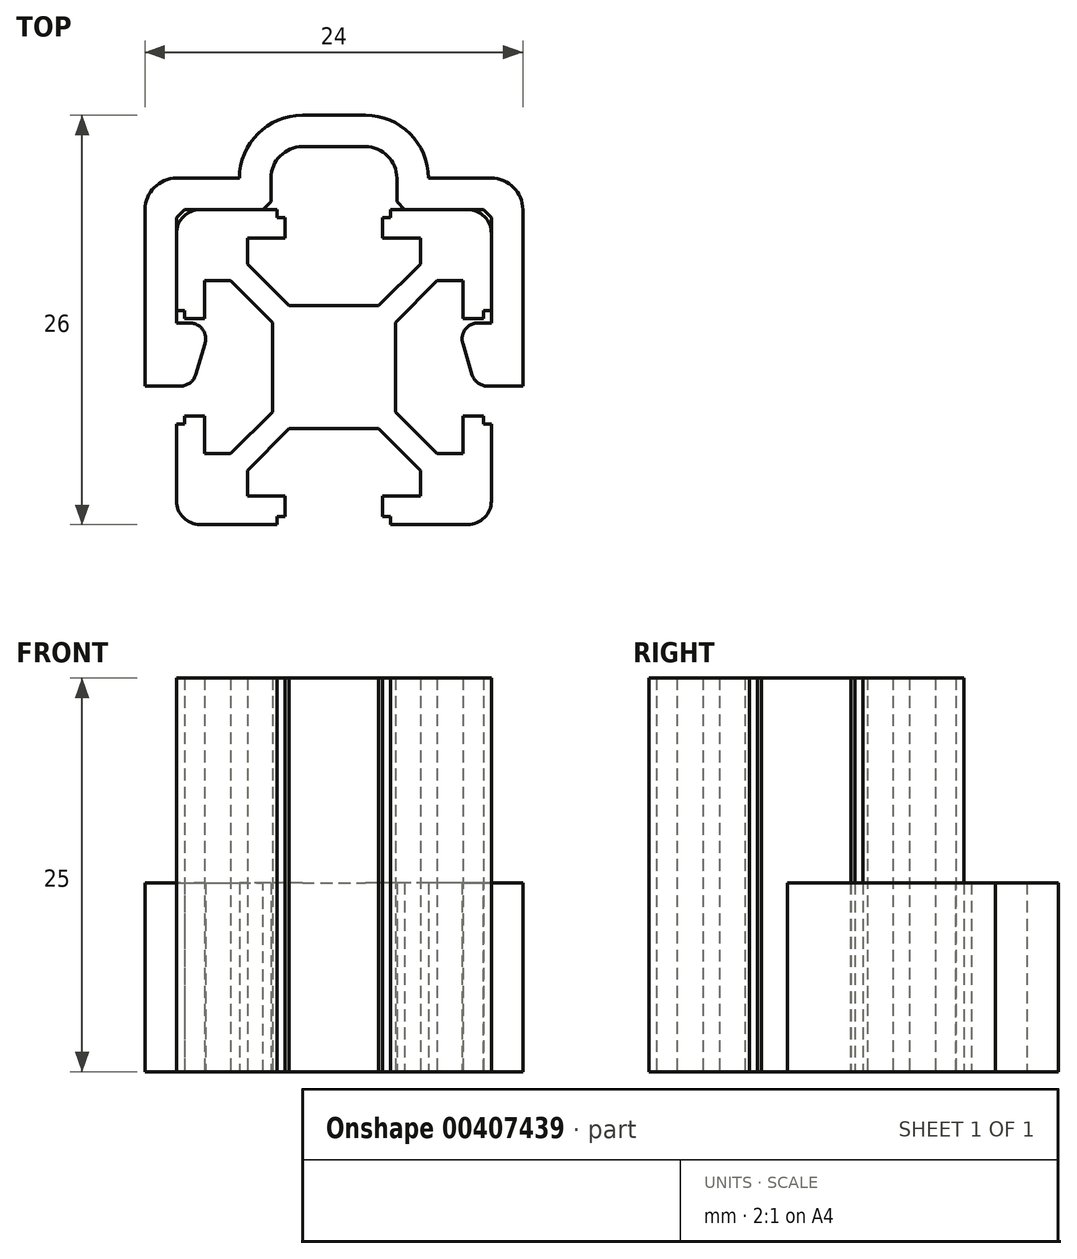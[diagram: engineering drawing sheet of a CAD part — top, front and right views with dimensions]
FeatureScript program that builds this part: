
annotation { "Feature Type Name" : "Feature", "Feature Type Description" : "" }
export const myFeature = defineFeature(function(context is Context, id is Id, definition is map)
    precondition{}
    {
        {
            var Q0;
            Q0=qCreatedBy(makeId("Top.planeOp"),FACE);
            var sketch = newSketch(context, id + "F0", { "sketchPlane" : qUnion([Q0])});
            skPoint(sketch, "E0", {"position": v(0, 0) * mm});
            skPoint(sketch, "E1", {"position": v(-3.9, 0) * mm});
            skLineSegment(sketch, "E2", {"start": v(-3.9, 0) * mm, "end": v(-3.9, 2.84) * mm});
            skLineSegment(sketch, "E3", {"start": v(-3.9, 2.84) * mm, "end": v(-6.56, 5.5) * mm});
            skLineSegment(sketch, "E4", {"start": v(-6.56, 5.5) * mm, "end": v(-8.2, 5.5) * mm});
            skLineSegment(sketch, "E5", {"start": v(-8.2, 5.5) * mm, "end": v(-8.2, 3.1) * mm});
            skLineSegment(sketch, "E6", {"start": v(-8.2, 3.1) * mm, "end": v(-9.5, 3.1) * mm});
            skLineSegment(sketch, "E7", {"start": v(-9.5, 3.1) * mm, "end": v(-9.5, 3.6) * mm});
            skLineSegment(sketch, "E8", {"start": v(-9.5, 3.6) * mm, "end": v(-10, 3.6) * mm});
            skLineSegment(sketch, "E9", {"start": v(-10, 3.6) * mm, "end": v(-10, 8.5) * mm});
            skLineSegment(sketch, "E10", {"start": v(-8.5, 10) * mm, "end": v(-3.6, 10) * mm});
            skLineSegment(sketch, "E11", {"start": v(-3.1, 9.5) * mm, "end": v(-3.1, 8.2) * mm});
            skLineSegment(sketch, "E12", {"start": v(-3.1, 8.2) * mm, "end": v(-5.5, 8.2) * mm});
            skLineSegment(sketch, "E13", {"start": v(-5.5, 8.2) * mm, "end": v(-5.5, 6.56) * mm});
            skLineSegment(sketch, "E14", {"start": v(-5.5, 6.56) * mm, "end": v(-2.84, 3.9) * mm});
            skLineSegment(sketch, "E15", {"start": v(-2.84, 3.9) * mm, "end": v(0, 3.9) * mm});
            skLineSegment(sketch, "E16", {"start": v(-3.6, 10) * mm, "end": v(-3.6, 9.5) * mm});
            skLineSegment(sketch, "E17", {"start": v(-3.6, 9.5) * mm, "end": v(-3.1, 9.5) * mm});
            skCircle(sketch, "E18", {"center": v(0, 0) * mm, "radius": 2.5 * mm});
            skPoint(sketch, "E19", {"position": v(0, 10) * mm});
            skPoint(sketch, "E19.positionSnap0", {"position": v(-6.8, 10) * mm});
            skPoint(sketch, "E20", {"position": v(-10, 0) * mm});
            skPoint(sketch, "E21.visualSharp", {"position": v(-10, 10) * mm});
            skArc(sketch, "E21.filletArc", {"start": v(-8.5, 10) * mm, "mid": v(-9.56, 9.56) * mm, "end": v(-10, 8.5) * mm});
            skPoint(sketch, "E22.visualSharp", {"position": v(-5.5, 6.56) * mm});
            skLineSegment(sketch, "E22.filletArc", {"start": v(-5.5, 6.56) * mm, "end": v(-5.5, 6.56) * mm});
            skPoint(sketch, "E23.visualSharp", {"position": v(-3.6, 10) * mm});
            skLineSegment(sketch, "E23.filletArc", {"start": v(-3.6, 10) * mm, "end": v(-3.6, 10) * mm});
            skPoint(sketch, "E24.visualSharp", {"position": v(-3.1, 9.5) * mm});
            skLineSegment(sketch, "E24.filletArc", {"start": v(-3.1, 9.5) * mm, "end": v(-3.1, 9.5) * mm});
            skPoint(sketch, "E25.visualSharp", {"position": v(-10, 3.6) * mm});
            skLineSegment(sketch, "E25.filletArc", {"start": v(-10, 3.6) * mm, "end": v(-10, 3.6) * mm});
            skLineSegment(sketch, "E26.1.0", {"start": v(-8.2, -3.1) * mm, "end": v(-8.2, -5.5) * mm});
            skLineSegment(sketch, "E26.1.1", {"start": v(-2.84, -3.9) * mm, "end": v(-5.5, -6.56) * mm});
            skLineSegment(sketch, "E26.1.2", {"start": v(0, -3.9) * mm, "end": v(-2.84, -3.9) * mm});
            skArc(sketch, "E26.1.3", {"start": v(-10, -8.5) * mm, "mid": v(-9.56, -9.56) * mm, "end": v(-8.5, -10) * mm});
            skLineSegment(sketch, "E26.1.4", {"start": v(-3.9, -2.84) * mm, "end": v(-3.9, 0) * mm});
            skPoint(sketch, "E26.1.5", {"position": v(0, -10) * mm});
            skPoint(sketch, "E26.1.7", {"position": v(-10, -10) * mm});
            skLineSegment(sketch, "E26.1.8", {"start": v(-5.5, -6.56) * mm, "end": v(-5.5, -8.2) * mm});
            skPoint(sketch, "E26.1.9", {"position": v(0, -3.9) * mm});
            skLineSegment(sketch, "E26.1.10", {"start": v(-6.56, -5.5) * mm, "end": v(-3.9, -2.84) * mm});
            skLineSegment(sketch, "E26.1.11", {"start": v(-8.2, -5.5) * mm, "end": v(-6.56, -5.5) * mm});
            skLineSegment(sketch, "E26.1.12", {"start": v(-9.5, -3.1) * mm, "end": v(-8.2, -3.1) * mm});
            skLineSegment(sketch, "E26.1.13", {"start": v(-5.5, -8.2) * mm, "end": v(-3.1, -8.2) * mm});
            skPoint(sketch, "E26.1.14", {"position": v(-10, -6.8) * mm});
            skLineSegment(sketch, "E26.1.15", {"start": v(-3.1, -8.2) * mm, "end": v(-3.1, -9.5) * mm});
            skLineSegment(sketch, "E26.1.17", {"start": v(-3.6, -10) * mm, "end": v(-8.5, -10) * mm});
            skLineSegment(sketch, "E26.1.18", {"start": v(-10, -8.5) * mm, "end": v(-10, -3.6) * mm});
            skPoint(sketch, "E26.1.19", {"position": v(-3.6, -10) * mm});
            skPoint(sketch, "E26.1.21", {"position": v(-9.5, -3.1) * mm});
            skPoint(sketch, "E26.1.22", {"position": v(-10, -3.6) * mm});
            skPoint(sketch, "E26.1.23", {"position": v(-6.56, -5.5) * mm});
            skLineSegment(sketch, "E26.1.24", {"start": v(-3.1, -9.5) * mm, "end": v(-3.6, -9.5) * mm});
            skLineSegment(sketch, "E26.1.25", {"start": v(-9.5, -3.6) * mm, "end": v(-9.5, -3.1) * mm});
            skLineSegment(sketch, "E26.1.26", {"start": v(-10, -3.6) * mm, "end": v(-9.5, -3.6) * mm});
            skLineSegment(sketch, "E26.1.27", {"start": v(-3.6, -9.5) * mm, "end": v(-3.6, -10) * mm});
            skLineSegment(sketch, "E26.2.0", {"start": v(3.1, -8.2) * mm, "end": v(5.5, -8.2) * mm});
            skLineSegment(sketch, "E26.2.1", {"start": v(3.9, -2.84) * mm, "end": v(6.56, -5.5) * mm});
            skLineSegment(sketch, "E26.2.2", {"start": v(3.9, 0) * mm, "end": v(3.9, -2.84) * mm});
            skArc(sketch, "E26.2.3", {"start": v(8.5, -10) * mm, "mid": v(9.56, -9.56) * mm, "end": v(10, -8.5) * mm});
            skLineSegment(sketch, "E26.2.4", {"start": v(2.84, -3.9) * mm, "end": v(0, -3.9) * mm});
            skPoint(sketch, "E26.2.5", {"position": v(10, 0) * mm});
            skPoint(sketch, "E26.2.6", {"position": v(0, -10) * mm});
            skPoint(sketch, "E26.2.7", {"position": v(10, -10) * mm});
            skLineSegment(sketch, "E26.2.8", {"start": v(6.56, -5.5) * mm, "end": v(8.2, -5.5) * mm});
            skPoint(sketch, "E26.2.9", {"position": v(3.9, 0) * mm});
            skLineSegment(sketch, "E26.2.10", {"start": v(5.5, -6.56) * mm, "end": v(2.84, -3.9) * mm});
            skLineSegment(sketch, "E26.2.11", {"start": v(5.5, -8.2) * mm, "end": v(5.5, -6.56) * mm});
            skLineSegment(sketch, "E26.2.12", {"start": v(3.1, -9.5) * mm, "end": v(3.1, -8.2) * mm});
            skLineSegment(sketch, "E26.2.13", {"start": v(8.2, -5.5) * mm, "end": v(8.2, -3.1) * mm});
            skPoint(sketch, "E26.2.14", {"position": v(6.8, -10) * mm});
            skLineSegment(sketch, "E26.2.15", {"start": v(8.2, -3.1) * mm, "end": v(9.5, -3.1) * mm});
            skLineSegment(sketch, "E26.2.17", {"start": v(10, -3.6) * mm, "end": v(10, -8.5) * mm});
            skLineSegment(sketch, "E26.2.18", {"start": v(8.5, -10) * mm, "end": v(3.6, -10) * mm});
            skPoint(sketch, "E26.2.19", {"position": v(10, -3.6) * mm});
            skPoint(sketch, "E26.2.21", {"position": v(3.1, -9.5) * mm});
            skPoint(sketch, "E26.2.22", {"position": v(3.6, -10) * mm});
            skPoint(sketch, "E26.2.23", {"position": v(5.5, -6.56) * mm});
            skLineSegment(sketch, "E26.2.24", {"start": v(9.5, -3.1) * mm, "end": v(9.5, -3.6) * mm});
            skLineSegment(sketch, "E26.2.25", {"start": v(3.6, -9.5) * mm, "end": v(3.1, -9.5) * mm});
            skLineSegment(sketch, "E26.2.26", {"start": v(3.6, -10) * mm, "end": v(3.6, -9.5) * mm});
            skLineSegment(sketch, "E26.2.27", {"start": v(9.5, -3.6) * mm, "end": v(10, -3.6) * mm});
            skLineSegment(sketch, "E26.3.0", {"start": v(8.2, 3.1) * mm, "end": v(8.2, 5.5) * mm});
            skLineSegment(sketch, "E26.3.1", {"start": v(2.84, 3.9) * mm, "end": v(5.5, 6.56) * mm});
            skLineSegment(sketch, "E26.3.2", {"start": v(0, 3.9) * mm, "end": v(2.84, 3.9) * mm});
            skArc(sketch, "E26.3.3", {"start": v(10, 8.5) * mm, "mid": v(9.56, 9.56) * mm, "end": v(8.5, 10) * mm});
            skLineSegment(sketch, "E26.3.4", {"start": v(3.9, 2.84) * mm, "end": v(3.9, 0) * mm});
            skPoint(sketch, "E26.3.6", {"position": v(10, 0) * mm});
            skPoint(sketch, "E26.3.7", {"position": v(10, 10) * mm});
            skLineSegment(sketch, "E26.3.8", {"start": v(5.5, 6.56) * mm, "end": v(5.5, 8.2) * mm});
            skPoint(sketch, "E26.3.9", {"position": v(0, 3.9) * mm});
            skLineSegment(sketch, "E26.3.10", {"start": v(6.56, 5.5) * mm, "end": v(3.9, 2.84) * mm});
            skLineSegment(sketch, "E26.3.11", {"start": v(8.2, 5.5) * mm, "end": v(6.56, 5.5) * mm});
            skLineSegment(sketch, "E26.3.12", {"start": v(9.5, 3.1) * mm, "end": v(8.2, 3.1) * mm});
            skLineSegment(sketch, "E26.3.13", {"start": v(5.5, 8.2) * mm, "end": v(3.1, 8.2) * mm});
            skPoint(sketch, "E26.3.14", {"position": v(10, 6.8) * mm});
            skLineSegment(sketch, "E26.3.15", {"start": v(3.1, 8.2) * mm, "end": v(3.1, 9.5) * mm});
            skLineSegment(sketch, "E26.3.17", {"start": v(3.6, 10) * mm, "end": v(8.5, 10) * mm});
            skLineSegment(sketch, "E26.3.18", {"start": v(10, 8.5) * mm, "end": v(10, 3.6) * mm});
            skPoint(sketch, "E26.3.19", {"position": v(3.6, 10) * mm});
            skPoint(sketch, "E26.3.21", {"position": v(9.5, 3.1) * mm});
            skPoint(sketch, "E26.3.22", {"position": v(10, 3.6) * mm});
            skPoint(sketch, "E26.3.23", {"position": v(6.56, 5.5) * mm});
            skLineSegment(sketch, "E26.3.24", {"start": v(3.1, 9.5) * mm, "end": v(3.6, 9.5) * mm});
            skLineSegment(sketch, "E26.3.25", {"start": v(9.5, 3.6) * mm, "end": v(9.5, 3.1) * mm});
            skLineSegment(sketch, "E26.3.26", {"start": v(10, 3.6) * mm, "end": v(9.5, 3.6) * mm});
            skLineSegment(sketch, "E26.3.27", {"start": v(3.6, 9.5) * mm, "end": v(3.6, 10) * mm});
            skSolve(sketch);
        }
        {
            var Q0;
            Q0=qCreatedBy(makeId("Top.planeOp"),FACE);
            var sketch = newSketch(context, id + "F1", { "sketchPlane" : qUnion([Q0]), "disableImprinting" : false});
            skLineSegment(sketch, "E27", {"start": v(0, -1.2) * mm, "end": v(0, 0) * mm, "construction": true});
            skLineSegment(sketch, "E28", {"start": v(0, -1.2) * mm, "end": v(-12, -1.2) * mm, "construction": true});
            skLineSegment(sketch, "E29", {"start": v(-12, -1.2) * mm, "end": v(-12, 10) * mm});
            skLineSegment(sketch, "E30", {"start": v(-10, 2.8) * mm, "end": v(-9.14, 2.8) * mm});
            skLineSegment(sketch, "E31", {"start": v(-9.74, -1.2) * mm, "end": v(-12, -1.2) * mm});
            skLineSegment(sketch, "E32", {"start": v(-8.19, 1.51) * mm, "end": v(-8.79, -0.49) * mm});
            skPoint(sketch, "E33.visualSharp", {"position": v(-9, -1.2) * mm});
            skArc(sketch, "E33.filletArc", {"start": v(-9.74, -1.2) * mm, "mid": v(-9.15, -1) * mm, "end": v(-8.79, -0.49) * mm});
            skPoint(sketch, "E34.visualSharp", {"position": v(-7.8, 2.8) * mm});
            skArc(sketch, "E34.filletArc", {"start": v(-8.19, 1.51) * mm, "mid": v(-8.34, 2.4) * mm, "end": v(-9.14, 2.8) * mm});
            skLineSegment(sketch, "E35", {"start": v(-10, 10) * mm, "end": v(-10, 2.8) * mm});
            skPoint(sketch, "E36", {"position": v(-10, 10) * mm});
            skLineSegment(sketch, "E37", {"start": v(-10, 10) * mm, "end": v(-4, 10) * mm});
            skLineSegment(sketch, "E38", {"start": v(-4, 10) * mm, "end": v(-4, 12) * mm});
            skLineSegment(sketch, "E39", {"start": v(-10, 12) * mm, "end": v(-6, 12) * mm});
            skLineSegment(sketch, "E40", {"start": v(-6, 12) * mm, "end": v(-6, 12) * mm});
            skLineSegment(sketch, "E41", {"start": v(-2, 16) * mm, "end": v(0, 16) * mm});
            skLineSegment(sketch, "E42", {"start": v(0, 14) * mm, "end": v(-2, 14) * mm});
            skLineSegment(sketch, "E43", {"start": v(-4, 12) * mm, "end": v(-4, 12) * mm});
            skPoint(sketch, "E44.visualSharp", {"position": v(-12, 12) * mm});
            skArc(sketch, "E44.filletArc", {"start": v(-10, 12) * mm, "mid": v(-11.41, 11.41) * mm, "end": v(-12, 10) * mm});
            skPoint(sketch, "E45.visualSharp", {"position": v(-4, 14) * mm});
            skArc(sketch, "E45.filletArc", {"start": v(-2, 14) * mm, "mid": v(-3.41, 13.41) * mm, "end": v(-4, 12) * mm});
            skPoint(sketch, "E46.visualSharp", {"position": v(-6, 16) * mm});
            skArc(sketch, "E46.filletArc", {"start": v(-2, 16) * mm, "mid": v(-4.83, 14.83) * mm, "end": v(-6, 12) * mm});
            skLineSegment(sketch, "E47.MirrorCS", {"start": v(9.74, -1.2) * mm, "end": v(12, -1.2) * mm});
            skLineSegment(sketch, "E48.MirrorCS", {"start": v(12, -1.2) * mm, "end": v(12, 10) * mm});
            skLineSegment(sketch, "E49.MirrorCS", {"start": v(6, 12) * mm, "end": v(6, 12) * mm});
            skPoint(sketch, "E50.MirrorP", {"position": v(10, 10) * mm});
            skPoint(sketch, "E51.MirrorP", {"position": v(7.8, 2.8) * mm});
            skArc(sketch, "E52.MirrorCS", {"start": v(2, 14) * mm, "mid": v(3.41, 13.41) * mm, "end": v(4, 12) * mm});
            skLineSegment(sketch, "E53.MirrorCS", {"start": v(10, 10) * mm, "end": v(10, 2.8) * mm});
            skLineSegment(sketch, "E54.MirrorCS", {"start": v(2, 16) * mm, "end": v(0, 16) * mm});
            skArc(sketch, "E55.MirrorCS", {"start": v(2, 16) * mm, "mid": v(4.83, 14.83) * mm, "end": v(6, 12) * mm});
            skArc(sketch, "E56.MirrorCS", {"start": v(9.74, -1.2) * mm, "mid": v(9.15, -1) * mm, "end": v(8.79, -0.49) * mm});
            skPoint(sketch, "E57.MirrorP", {"position": v(4, 14) * mm});
            skPoint(sketch, "E58.MirrorP", {"position": v(6, 16) * mm});
            skPoint(sketch, "E59.MirrorP", {"position": v(12, 12) * mm});
            skLineSegment(sketch, "E60.MirrorCS", {"start": v(10, 12) * mm, "end": v(6, 12) * mm});
            skLineSegment(sketch, "E61.MirrorCS", {"start": v(4, 12) * mm, "end": v(4, 12) * mm});
            skArc(sketch, "E62.MirrorCS", {"start": v(8.19, 1.51) * mm, "mid": v(8.34, 2.4) * mm, "end": v(9.14, 2.8) * mm});
            skArc(sketch, "E63.MirrorCS", {"start": v(10, 12) * mm, "mid": v(11.41, 11.41) * mm, "end": v(12, 10) * mm});
            skLineSegment(sketch, "E64.MirrorCS", {"start": v(10, 10) * mm, "end": v(4, 10) * mm});
            skPoint(sketch, "E65.MirrorP", {"position": v(9, -1.2) * mm});
            skLineSegment(sketch, "E66.MirrorCS", {"start": v(4, 10) * mm, "end": v(4, 12) * mm});
            skLineSegment(sketch, "E67.MirrorCS", {"start": v(0, -1.2) * mm, "end": v(12, -1.2) * mm, "construction": true});
            skLineSegment(sketch, "E68.MirrorCS", {"start": v(10, 2.8) * mm, "end": v(9.14, 2.8) * mm});
            skLineSegment(sketch, "E69.MirrorCS", {"start": v(8.19, 1.51) * mm, "end": v(8.79, -0.49) * mm});
            skLineSegment(sketch, "E70.MirrorCS", {"start": v(0, 14) * mm, "end": v(2, 14) * mm});
            skLineSegment(sketch, "E71", {"start": v(4, 10) * mm, "end": v(-4, 10) * mm, "construction": true});
            skSolve(sketch);
        }
        {
            var Q0;
            Q0=makeQuery(id+"F1.imprint","IMPRINT",FACE,{"disambiguationData":[TD([[makeQuery(id+"F1.imprint","IMPRINT",EDGE,{"derivedFrom":sQuery(id+"F1.wireOp",EDGE,"E29")}),-1.0]])]});
            var Q1;
            Q1=makeQuery(id+"F1.imprint","IMPRINT",FACE,{"disambiguationData":[TD([[makeQuery(id+"F1.imprint","IMPRINT",EDGE,{"derivedFrom":sQuery(id+"F1.wireOp",EDGE,"E47.MirrorCS")}),1.0]])]});
            var Q2;
            Q2=makeQuery(id+"F1.imprint","IMPRINT",FACE,{"disambiguationData":[TD([[makeQuery(id+"F1.imprint","IMPRINT",EDGE,{"derivedFrom":sQuery(id+"F1.wireOp",EDGE,"E41")}),-1.0]])]});
            extrude(context, id + "F2", {"entities" : qUnion([Q0, Q1, Q2]), "depth" : 12 * mm});
        }
        {
            var Q0;
            Q0=makeQuery(id+"F2.opExtrude","SWEPT_EDGE",EDGE,{"disambiguationData":[OSD([sQuery(id+"F1.wireOp",EDGE,"E35"),sQuery(id+"F1.wireOp",EDGE,"E37")])]});
            var Q1;
            Q1=makeQuery(id+"F2.opExtrude","SWEPT_EDGE",EDGE,{"disambiguationData":[OSD([sQuery(id+"F1.wireOp",EDGE,"E53.MirrorCS"),sQuery(id+"F1.wireOp",EDGE,"E64.MirrorCS")])]});
            var Q2;
            Q2=makeQuery(id+"F2.opExtrude","SWEPT_EDGE",EDGE,{"disambiguationData":[OSD([sQuery(id+"F1.wireOp",EDGE,"E64.MirrorCS"),sQuery(id+"F1.wireOp",EDGE,"E66.MirrorCS")])]});
            var Q3;
            Q3=makeQuery(id+"F2.opExtrude","SWEPT_EDGE",EDGE,{"disambiguationData":[OSD([sQuery(id+"F1.wireOp",EDGE,"E37"),sQuery(id+"F1.wireOp",EDGE,"E38")])]});
            chamfer(context, id + "F3", {"entities" : qUnion([Q0, Q1, Q2, Q3]), "width" : .5 * mm, "tangentPropagation" : true});
        }
        {
            var Q0;
            Q0=makeQuery(id+"F0.imprint","IMPRINT",FACE,{"disambiguationData":[TD([[makeQuery(id+"F0.imprint","IMPRINT",EDGE,{"derivedFrom":sQuery(id+"F0.wireOp",EDGE,"E18")}),1.0]])]});
            var Q1;
            Q1=makeQuery(id+"F0.imprint","IMPRINT",FACE,{"disambiguationData":[TD([[makeQuery(id+"F0.imprint","IMPRINT",EDGE,{"derivedFrom":sQuery(id+"F0.wireOp",EDGE,"E2")}),-1.0]])]});
            extrude(context, id + "F4", {"entities" : qUnion([Q0, Q1]), "depth" : 25 * mm});
        }
    });
